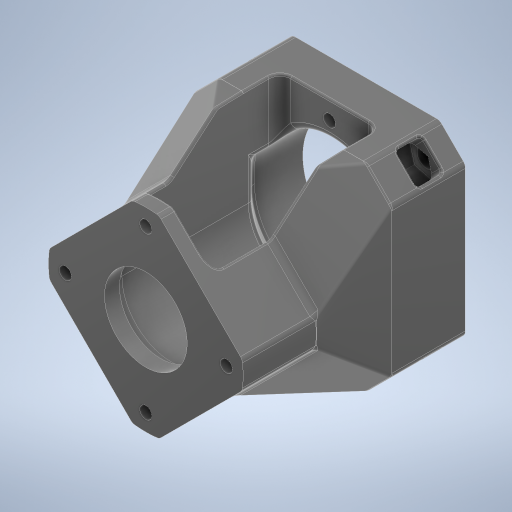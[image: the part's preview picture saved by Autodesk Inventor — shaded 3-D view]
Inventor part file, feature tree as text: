
AUTODESK INVENTOR PART (.ipt)
format: ipt  version: 2024 (Build 280153000, 153)  size: 1,261,568 bytes
history: native  units: mm
features: sketch x13, fillet x10, extrude x9, projected_geometry x7, plane x3, hole x3, other x2, loft x1, chamfer x1, pattern_circular x1
ambient origin geometry x8: Origin, YZ Plane, XZ Plane, XY Plane, X Axis, Y Axis, Z Axis, Center Point
bodies: Solid1 (feature_tree)
feature tree (50):
  extrude  "Extrusion1"  Depth=40.0mm
  plane  "Work Plane1"
  extrude  "Extrusion3"  Depth=42.0mm
  fillet  "Fillet3"  Radius=42.0mm
  fillet  "Fillet4"  Radius=42.0mm
  sketch  "Sketch7"  dims[d6=52.0mm d8=54.0mm]
  sketch  "Sketch8"  dims[d9=20.0mm d10=0.0mm d43=7.0mm]
  loft  "Loft1"
  extrude  "Extrusion4"  Depth=7.0mm
  extrude  "Extrusion5"  Depth=7.0mm
  sketch  "Sketch11"  dims[d48=7.0mm d49=7.0mm d50=7.0mm d51=7.0mm]
  extrude  "Extrusion6"  Depth=7.0mm
  sketch  "Sketch12"  dims[d52=6.0mm]
  extrude  "Extrusion7"  Depth=7.0mm
  fillet  "Fillet12"  Radius=7.0mm
  fillet  "Fillet5"  Radius=7.0mm
  chamfer  "Chamfer2"  Distance=20.0mm
  fillet  "Fillet6"  Radius=2.0mm
  fillet  "Fillet7"  Radius=2.0mm
  fillet  "Fillet13"  [1 undecoded]
  fillet  "Fillet14"  Radius=34.5mm
  hole  "Hole4"  [1 undecoded]
  sketch  "Sketch14"  dims[d54=-60.0mm]
  extrude  "Extrusion8"  Depth=0.5mm
  extrude  "Extrusion9"  Depth=0.5mm TaperAngle=0.0deg
  pattern_circular  "Circular Pattern1"  [2 undecoded]
  fillet  "Fillet11"  Radius=4.0mm
  hole  "Hole5"  [1 undecoded]
  plane  "Work Plane3"
  hole  "Hole6"  [1 undecoded]
  fillet  "Fillet15"  Radius=3.75mm
  plane  "Work Plane2"
  extrude  "Extrusion10"  Depth=0.5mm
  sketch  "Sketch1"  dims[d0=110.0mm d1=40.0mm]
  sketch  "Sketch6"  dims[d2=42.0mm d3=42.0mm d4=42.0mm d5=42.0mm]
  projected_geometry  "Projected Loop1"
  projected_geometry  "Projected Loop2"
  sketch  "Sketch9"  dims[d44=7.0mm d45=7.0mm]
  sketch  "Sketch10"  dims[d46=7.0mm d47=7.0mm]
  projected_geometry  "Projected Loop3"
  sketch  "Sketch13"  dims[d53=6.0mm]
  projected_geometry  "Projected Loop4"
  sketch  "Sketch15"  dims[d55=42.3mm]
  sketch  "Sketch17"  dims[d56=42.3mm]
  other  "Edges1"
  other  "Edges2"
  sketch  "Sketch18"  dims[d57=53.0mm d58=20.0mm d59=0.0mm d60=2.0mm d61=2.0mm d62=0.0mm d63=90.0deg d64=0.0mm d65=90.0deg d66=34.5mm d67=14.0mm d68=0.0mm d69=22.5mm d70=4.0mm d71=0.0mm d72=27.0mm d73=4.0mm d74=0.0mm d75=4.0mm d76=0.0mm d80=3.0mm d81=3.75mm d82=2.0mm d83=45.0deg d84=2.0mm d85=2.0mm d88=38.0mm d89=38.0mm d90=5.3mm d91=6.0mm d92=4.0mm d93=2.0mm d94=90.0deg d95=12.5mm d96=0.0mm d97=8.22mm d99=2.0mm d100=7.0mm d101=0.0mm d102=10.0mm d103=0.0mm d105=40.0mm d106=360.0deg d108=1.0mm d111=3.3mm d112=6.0mm d113=4.0mm d114=2.0mm d115=90.0deg d116=17.0mm d117=0.0mm d119=-5.0mm d120=6.5mm d121=12.0mm d122=0.0mm d123=27.0mm d124=5.0mm d125=4.0mm d126=1.0mm d127=0.5mm d128=31.0mm d129=-4.0mm d131=6.5mm d132=6.0mm d133=4.0mm d134=2.0mm d135=90.0deg d136=8.0mm d137=0.0mm d138=0.5mm d17=1.0mm d18=1.0mm d19=1.0mm d20=0.15mm d21=0.25mm d22=0.375mm d23=14.3117mm d24=0.75mm d25=20.594885mm d26=0.0625mm d27=0.75mm d28=0.375mm d107=0.5mm]
  projected_geometry  "Project Cut Edges1"
  projected_geometry  "Project Cut Edges2"
  projected_geometry  "Project Cut Edges3"
note: 6 required parameter values undecoded (feature->parameter linkage not recoverable at this tier; creation-order binding heuristic only, values carry confidence <= 0.55)
